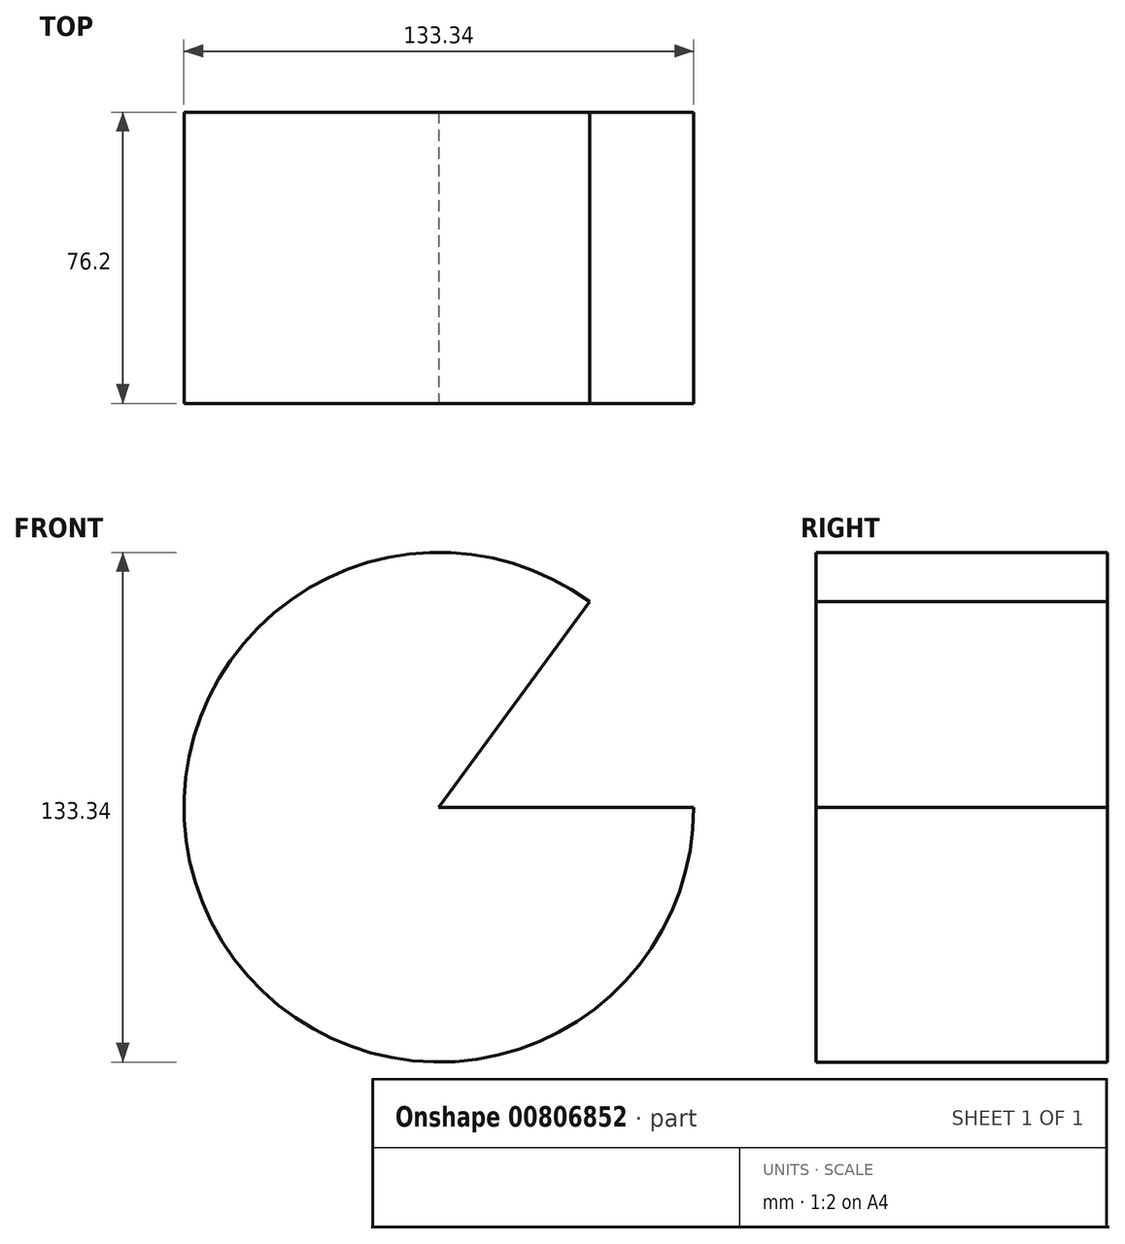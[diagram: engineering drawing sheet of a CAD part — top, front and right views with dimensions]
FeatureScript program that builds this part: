
annotation { "Feature Type Name" : "Feature", "Feature Type Description" : "" }
export const myFeature = defineFeature(function(context is Context, id is Id, definition is map)
    precondition{}
    {
        {
            var Q0;
            Q0=qCreatedBy(makeId("Front.planeOp"),FACE);
            var sketch = newSketch(context, id + "F0", { "sketchPlane" : qUnion([Q0])});
            skCircle(sketch, "E0", {"center": v(0, 0) * mm, "radius": 66.67 * mm});
            skSolve(sketch);
        }
        {
            var Q0;
            Q0 = qSketchRegion(id + "F0", true);
            extrude(context, id + "F1", {"entities" : qUnion([Q0]), "endBound" : BoundingType.SYMMETRIC, "depth" : 76.2 * mm, "offsetDistance" : 25.4 * mm});
        }
        {
            var Q0;
            Q0=makeQuery(id+"F1.opExtrude","CAP_FACE",FACE,{"disambiguationData":[OSD([sQuery(id+"F0.wireOp",EDGE,"E0")])],"isStart":false});
            var sketch = newSketch(context, id + "F2", { "sketchPlane" : qUnion([Q0])});
            skLineSegment(sketch, "E1", {"start": v(0, 0) * mm, "end": v(66.67, 0) * mm});
            skLineSegment(sketch, "E2", {"start": v(0, 0) * mm, "end": v(39.44, 53.75) * mm});
            skSolve(sketch);
        }
        {
            var Q0;
            Q0 = qSketchRegion(id + "F2", true);
            var Q1;
            {var subQ0=sQuery(id+"F2.wireOp",EDGE,"E1");Q1=makeQuery(id+"F2.imprint","IMPRINT",FACE,{"disambiguationData":[TD([[makeQuery(id+"F2.imprint","IMPRINT",EDGE,{"derivedFrom":subQ0}),1.0]])]});}
            extrude(context, id + "F3", {"entities" : qUnion([Q0, Q1]), "operationType" : NewBodyOperationType.REMOVE, "endBound" : BoundingType.THROUGH_ALL, "oppositeDirection" : true, "depth" : 25.4 * mm, "offsetDistance" : 25.4 * mm});
        }
    });
